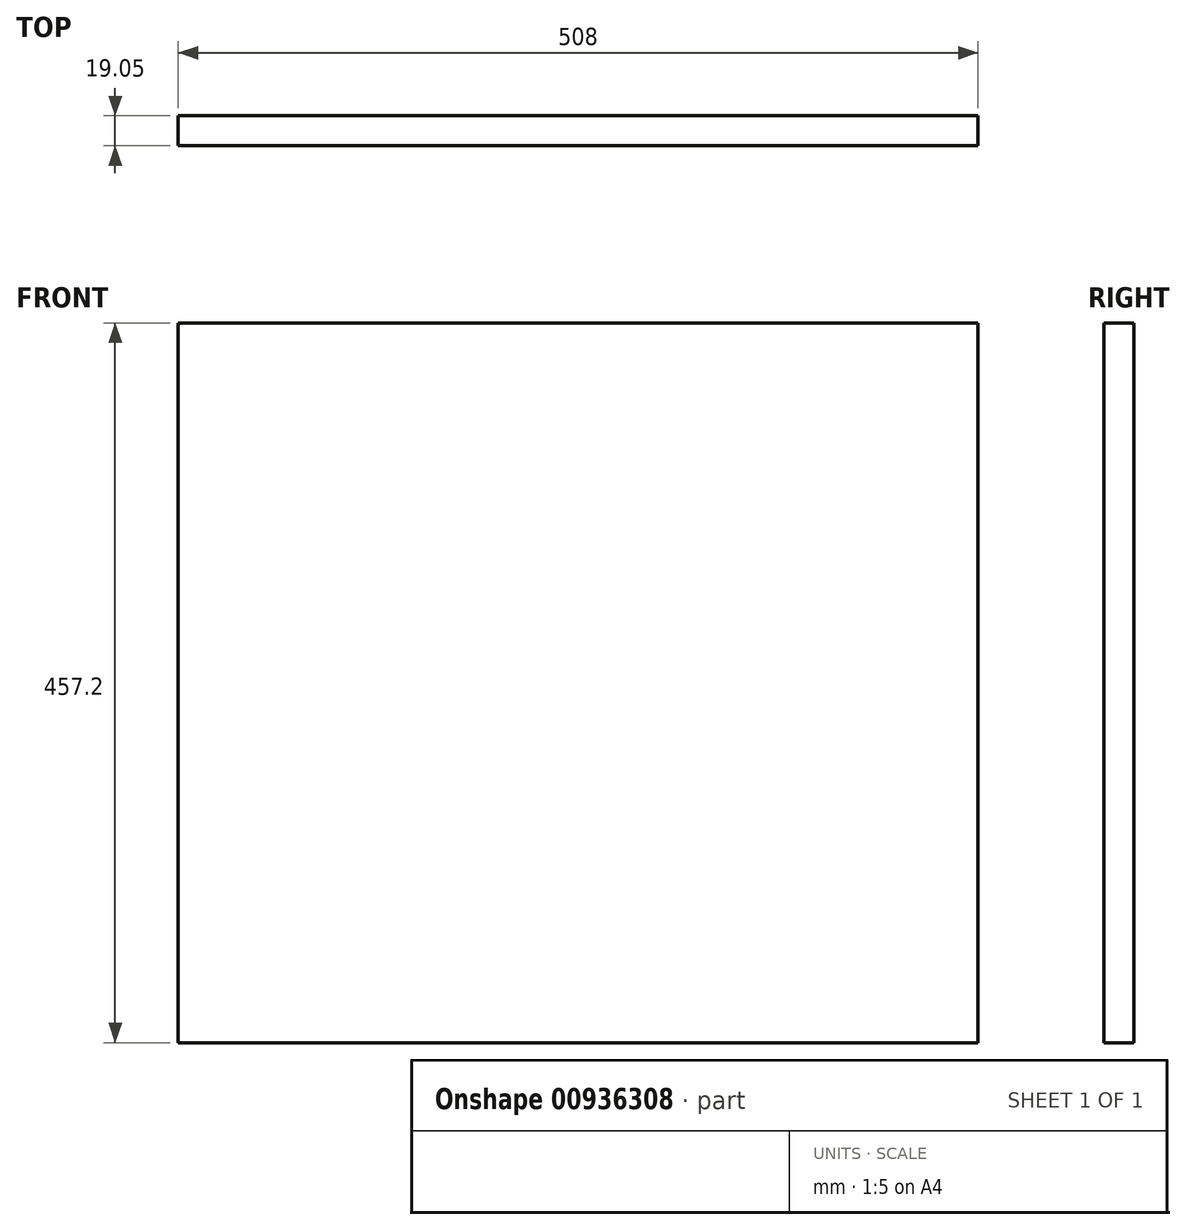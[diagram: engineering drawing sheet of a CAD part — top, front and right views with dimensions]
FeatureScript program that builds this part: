
annotation { "Feature Type Name" : "Feature", "Feature Type Description" : "" }
export const myFeature = defineFeature(function(context is Context, id is Id, definition is map)
    precondition{}
    {
        {
            var Q0;
            Q0=qCreatedBy(makeId("Front.planeOp"),FACE);
            var sketch = newSketch(context, id + "F0", { "sketchPlane" : qUnion([Q0])});
            skLineSegment(sketch, "E0.bottom", {"start": v(254, 228.6) * mm, "end": v(-254, 228.6) * mm});
            skLineSegment(sketch, "E0.top", {"start": v(254, -228.6) * mm, "end": v(-254, -228.6) * mm});
            skLineSegment(sketch, "E0.left", {"start": v(254, 228.6) * mm, "end": v(254, -228.6) * mm});
            skLineSegment(sketch, "E0.right", {"start": v(-254, 228.6) * mm, "end": v(-254, -228.6) * mm});
            skPoint(sketch, "E0.middle", {"position": v(0, 0) * mm});
            skSolve(sketch);
        }
        {
            var Q0;
            Q0=makeQuery(id+"F0.imprint","IMPRINT",FACE,{"disambiguationData":[TD([[makeQuery(id+"F0.imprint","IMPRINT",EDGE,{"derivedFrom":sQuery(id+"F0.wireOp",EDGE,"E0.bottom")}),1.0]])]});
            extrude(context, id + "F1", {"entities" : qUnion([Q0]), "depth" : 19.05 * mm, "offsetDistance" : 25.4 * mm});
        }
    });
